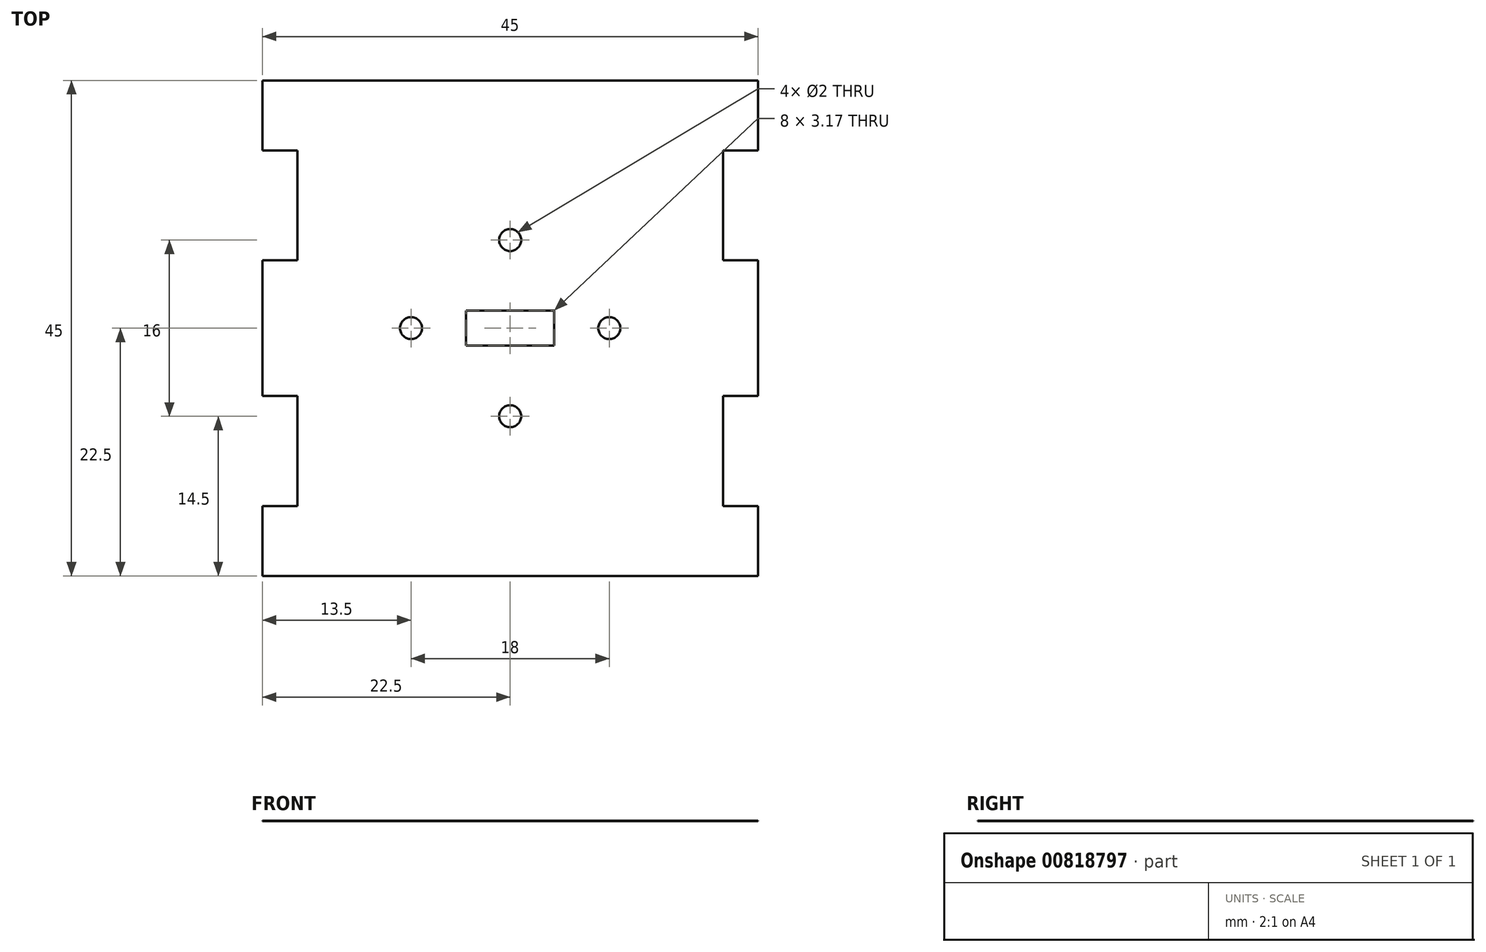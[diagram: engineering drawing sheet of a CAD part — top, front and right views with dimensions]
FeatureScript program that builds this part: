
annotation { "Feature Type Name" : "Feature", "Feature Type Description" : "" }
export const myFeature = defineFeature(function(context is Context, id is Id, definition is map)
    precondition{}
    {
        {
            var Q0;
            Q0=qCreatedBy(makeId("Top.planeOp"),FACE);
            var sketch = newSketch(context, id + "F0", { "sketchPlane" : qUnion([Q0])});
            skLineSegment(sketch, "E0.bottom", {"start": v(22.5, -22.5) * mm, "end": v(-22.5, -22.5) * mm});
            skLineSegment(sketch, "E0.top", {"start": v(22.5, 22.5) * mm, "end": v(-22.5, 22.5) * mm});
            skPoint(sketch, "E0.middle", {"position": v(0, 0) * mm});
            skLineSegment(sketch, "E1.bottom", {"start": v(-22.5, 16.15) * mm, "end": v(-19.33, 16.15) * mm});
            skLineSegment(sketch, "E1.top", {"start": v(-22.5, 6.15) * mm, "end": v(-19.33, 6.15) * mm});
            skLineSegment(sketch, "E1.right", {"start": v(-19.33, 16.15) * mm, "end": v(-19.33, 6.15) * mm});
            skLineSegment(sketch, "E2.bottom", {"start": v(-22.5, -6.15) * mm, "end": v(-19.32, -6.15) * mm});
            skLineSegment(sketch, "E2.top", {"start": v(-22.5, -16.15) * mm, "end": v(-19.32, -16.15) * mm});
            skLineSegment(sketch, "E2.right", {"start": v(-19.32, -6.15) * mm, "end": v(-19.32, -16.15) * mm});
            skLineSegment(sketch, "E3.bottom", {"start": v(22.5, 16.15) * mm, "end": v(19.33, 16.15) * mm});
            skLineSegment(sketch, "E3.top", {"start": v(22.5, 6.15) * mm, "end": v(19.33, 6.15) * mm});
            skLineSegment(sketch, "E3.right", {"start": v(19.33, 16.15) * mm, "end": v(19.33, 6.15) * mm});
            skLineSegment(sketch, "E4.bottom", {"start": v(22.5, -6.15) * mm, "end": v(19.33, -6.15) * mm});
            skLineSegment(sketch, "E4.top", {"start": v(22.5, -16.15) * mm, "end": v(19.33, -16.15) * mm});
            skLineSegment(sketch, "E4.right", {"start": v(19.33, -6.15) * mm, "end": v(19.33, -16.15) * mm});
            skLineSegment(sketch, "E5", {"start": v(-22.5, 11.15) * mm, "end": v(22.5, 11.15) * mm});
            skPoint(sketch, "E6", {"position": v(-19.33, 11.15) * mm});
            skPoint(sketch, "E7", {"position": v(19.33, 11.15) * mm});
            skPoint(sketch, "E8", {"position": v(-19.32, -11.15) * mm});
            skPoint(sketch, "E9", {"position": v(19.33, -11.15) * mm});
            skLineSegment(sketch, "E10", {"start": v(-22.5, -11.15) * mm, "end": v(22.5, -11.15) * mm});
            skCircle(sketch, "E11", {"center": v(-9, 0) * mm, "radius": 1 * mm});
            skCircle(sketch, "E12", {"center": v(9, 0) * mm, "radius": 1 * mm});
            skLineSegment(sketch, "E13.bottom", {"start": v(4, 1.59) * mm, "end": v(-4, 1.59) * mm});
            skLineSegment(sketch, "E13.top", {"start": v(4, -1.59) * mm, "end": v(-4, -1.59) * mm});
            skLineSegment(sketch, "E13.left", {"start": v(4, 1.59) * mm, "end": v(4, -1.59) * mm});
            skLineSegment(sketch, "E13.right", {"start": v(-4, 1.59) * mm, "end": v(-4, -1.59) * mm});
            skCircle(sketch, "E14", {"center": v(0, 0) * mm, "radius": 9 * mm});
            skCircle(sketch, "E15", {"center": v(0, 0) * mm, "radius": 8 * mm});
            skCircle(sketch, "E16", {"center": v(0, 8) * mm, "radius": 1 * mm});
            skCircle(sketch, "E17", {"center": v(0, -8) * mm, "radius": 1 * mm});
            skLineSegment(sketch, "E18", {"start": v(-22.5, 22.5) * mm, "end": v(-22.5, 16.15) * mm});
            skLineSegment(sketch, "E19", {"start": v(-22.5, 6.15) * mm, "end": v(-22.5, -6.15) * mm});
            skLineSegment(sketch, "E20", {"start": v(-22.5, -16.15) * mm, "end": v(-22.5, -22.5) * mm});
            skLineSegment(sketch, "E21", {"start": v(22.5, -16.15) * mm, "end": v(22.5, -22.5) * mm});
            skLineSegment(sketch, "E22", {"start": v(22.5, -6.15) * mm, "end": v(22.5, 6.15) * mm});
            skLineSegment(sketch, "E23", {"start": v(22.5, 16.15) * mm, "end": v(22.5, 22.5) * mm});
            skSolve(sketch);
        }
        {
            var Q0;
            {var subQ12=sQuery(id+"F0.wireOp",EDGE,"E1.bottom");Q0=makeQuery(id+"F0.imprint","IMPRINT",FACE,{"disambiguationData":[TD([[makeQuery(id+"F0.imprint","IMPRINT",EDGE,{"derivedFrom":subQ12}),1.0]])]});}
            var Q1;
            {var subQ13=sQuery(id+"F0.wireOp",EDGE,"E1.top");Q1=makeQuery(id+"F0.imprint","IMPRINT",FACE,{"disambiguationData":[TD([[makeQuery(id+"F0.imprint","IMPRINT",EDGE,{"derivedFrom":subQ13}),-1.0]])]});}
            var Q2;
            {var subQ2=sQuery(id+"F0.wireOp",EDGE,"E0.bottom");Q2=makeQuery(id+"F0.imprint","IMPRINT",FACE,{"disambiguationData":[TD([[makeQuery(id+"F0.imprint","IMPRINT",EDGE,{"derivedFrom":subQ2}),-1.0]])]});}
            var Q3;
            {var subQ5=sQuery(id+"F0.wireOp",EDGE,"XshcXygI-ylaP-oBMM-9xMQ-7iAmNTYONi5N");Q3=makeQuery(id+"F0.imprint","IMPRINT",FACE,{"disambiguationData":[TD([[makeQuery(id+"F0.imprint","IMPRINT",EDGE,{"derivedFrom":subQ5}),1.0]])]});}
            var Q4;
            {var subQ0=sQuery(id+"F0.wireOp",EDGE,"E11");var subQ1=sQuery(id+"F0.wireOp",EDGE,"M3YKA7js-OKau-kGR6-5s4F-Iv9aHX7OsuaV");var subQ2=makeQuery(id+"F0.imprint","INTERSECT",VERTEX,{"disambiguationData":[OD(0.0)],"derivedFrom":[subQ1,subQ0]});Q4=makeQuery(id+"F0.imprint","IMPRINT",FACE,{"disambiguationData":[TD([[makeQuery(id+"F0.imprint","IMPRINT",EDGE,{"disambiguationData":[TD([[subQ2,1.0]])],"derivedFrom":subQ1}),1.0]])]});}
            var Q5;
            Q5=makeQuery(id+"F0.imprint","IMPRINT",FACE,{"disambiguationData":[TD([[makeQuery(id+"F0.imprint","IMPRINT",EDGE,{"derivedFrom":sQuery(id+"F0.wireOp",EDGE,"E13.bottom")}),-1.0]])]});
            var Q6;
            {var subQ0=sQuery(id+"F0.wireOp",EDGE,"E14");var subQ1=sQuery(id+"F0.wireOp",EDGE,"E11");var subQ2=makeQuery(id+"F0.imprint","INTERSECT",VERTEX,{"disambiguationData":[OD(0.0)],"derivedFrom":[subQ1,subQ0]});Q6=makeQuery(id+"F0.imprint","IMPRINT",FACE,{"disambiguationData":[TD([[makeQuery(id+"F0.imprint","IMPRINT",EDGE,{"disambiguationData":[TD([[subQ2,1.0]])],"derivedFrom":subQ1}),-1.0]])]});}
            var Q7;
            {var subQ0=sQuery(id+"F0.wireOp",EDGE,"E15");var subQ1=sQuery(id+"F0.wireOp",EDGE,"E12");var subQ2=makeQuery(id+"F0.imprint","INTERSECT",VERTEX,{"derivedFrom":[subQ1,subQ0]});Q7=makeQuery(id+"F0.imprint","IMPRINT",FACE,{"disambiguationData":[TD([[makeQuery(id+"F0.imprint","IMPRINT",EDGE,{"disambiguationData":[TD([[subQ2,1.0]])],"derivedFrom":subQ1}),-1.0]])]});}
            var Q8;
            {var subQ0=sQuery(id+"F0.wireOp",EDGE,"E15");var subQ1=sQuery(id+"F0.wireOp",EDGE,"E12");var subQ2=makeQuery(id+"F0.imprint","INTERSECT",VERTEX,{"derivedFrom":[subQ1,subQ0]});Q8=makeQuery(id+"F0.imprint","IMPRINT",FACE,{"disambiguationData":[TD([[makeQuery(id+"F0.imprint","IMPRINT",EDGE,{"disambiguationData":[TD([[subQ2,-1.0]])],"derivedFrom":subQ1}),-1.0]])]});}
            var Q9;
            {var subQ0=sQuery(id+"F0.wireOp",EDGE,"E15");var subQ1=sQuery(id+"F0.wireOp",EDGE,"E11");var subQ2=makeQuery(id+"F0.imprint","INTERSECT",VERTEX,{"derivedFrom":[subQ1,subQ0]});Q9=makeQuery(id+"F0.imprint","IMPRINT",FACE,{"disambiguationData":[TD([[makeQuery(id+"F0.imprint","IMPRINT",EDGE,{"disambiguationData":[TD([[subQ2,1.0]])],"derivedFrom":subQ1}),-1.0]])]});}
            extrude(context, id + "F1", {"entities" : qUnion([Q0, Q1, Q2, Q3, Q4, Q5, Q6, Q7, Q8, Q9]), "depth" : 1 / 203.2 * mm, "offsetDistance" : 25 * mm});
        }
    });
